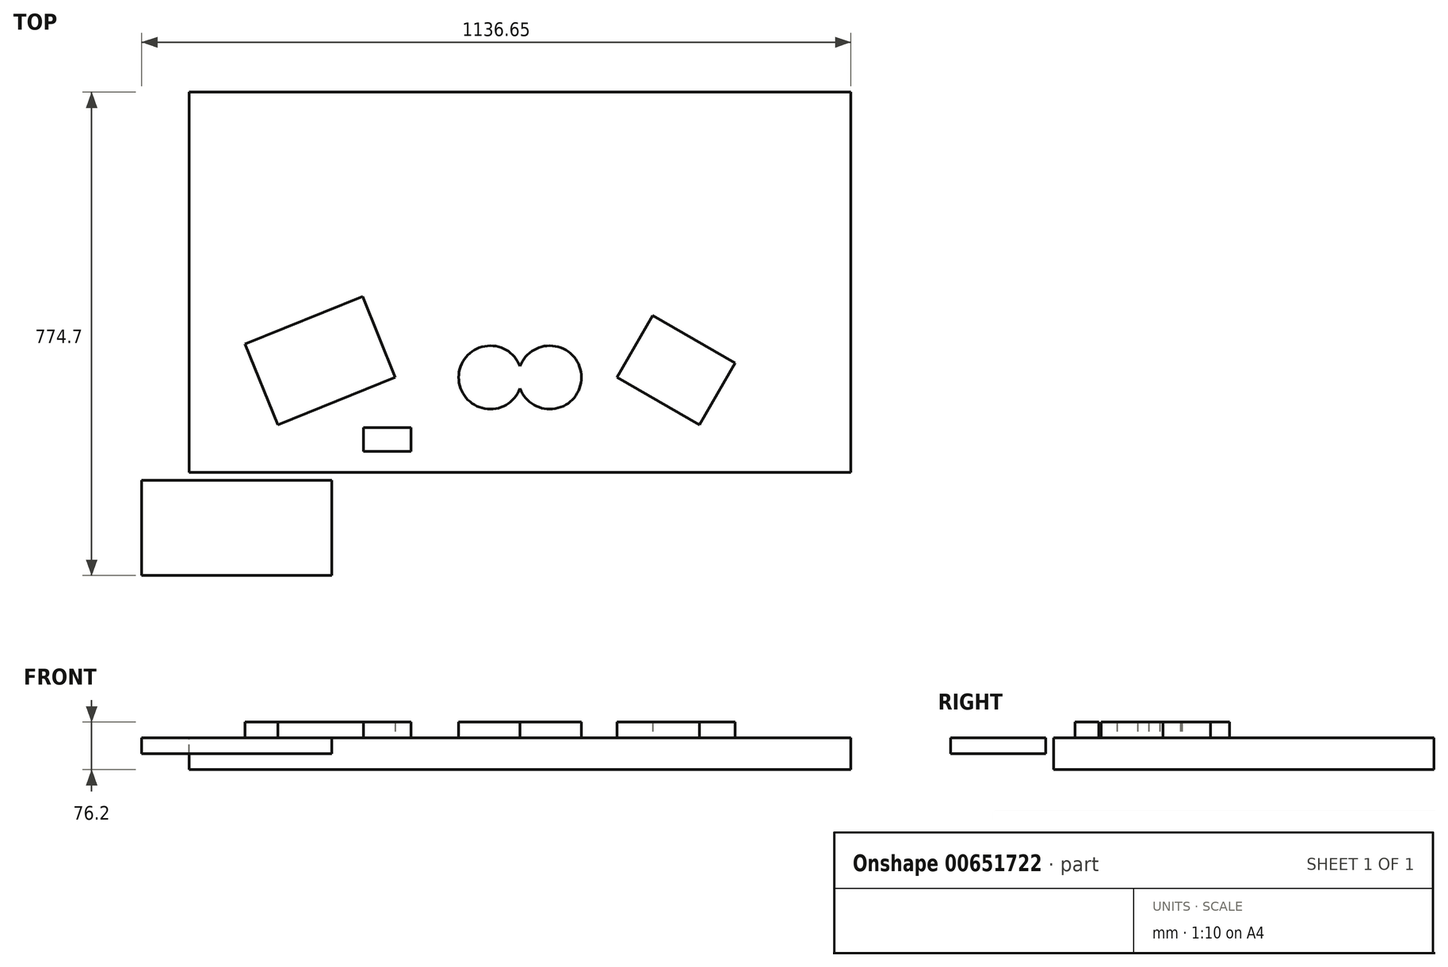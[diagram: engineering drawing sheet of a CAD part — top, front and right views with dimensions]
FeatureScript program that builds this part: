
annotation { "Feature Type Name" : "Feature", "Feature Type Description" : "" }
export const myFeature = defineFeature(function(context is Context, id is Id, definition is map)
    precondition{}
    {
        {
            var Q0;
            Q0=qCreatedBy(makeId("Top.planeOp"),FACE);
            var sketch = newSketch(context, id + "F0", { "sketchPlane" : qUnion([Q0])});
            skLineSegment(sketch, "E0.bottom", {"start": v(0, 0) * mm, "end": v(1060.45, 0) * mm});
            skLineSegment(sketch, "E0.top", {"start": v(0, 609.6) * mm, "end": v(1060.45, 609.6) * mm});
            skLineSegment(sketch, "E0.left", {"start": v(0, 0) * mm, "end": v(0, 609.6) * mm});
            skLineSegment(sketch, "E0.right", {"start": v(1060.45, 0) * mm, "end": v(1060.45, 609.6) * mm});
            skPoint(sketch, "E1", {"position": v(530.22, 0) * mm});
            skPoint(sketch, "E2", {"position": v(1060.45, 124.87) * mm});
            skPoint(sketch, "E3", {"position": v(1060.45, 302.67) * mm});
            skSolve(sketch);
        }
        {
            var Q0;
            Q0=makeQuery(id+"F0.imprint","IMPRINT",FACE,{"disambiguationData":[TD([[makeQuery(id+"F0.imprint","IMPRINT",EDGE,{"derivedFrom":sQuery(id+"F0.wireOp",EDGE,"E0.bottom")}),1.0]])]});
            var sketch = newSketch(context, id + "F1", { "sketchPlane" : qUnion([Q0])});
            skPoint(sketch, "E4", {"position": v(89.44, 205.7) * mm});
            skPoint(sketch, "E5", {"position": v(141.83, 76.2) * mm});
            skPoint(sketch, "E6", {"position": v(330.2, 152.4) * mm});
            skPoint(sketch, "E7", {"position": v(277.81, 281.9) * mm});
            skLineSegment(sketch, "E8", {"start": v(277.81, 281.9) * mm, "end": v(330.2, 152.4) * mm});
            skLineSegment(sketch, "E9", {"start": v(141.83, 76.2) * mm, "end": v(330.2, 152.4) * mm});
            skLineSegment(sketch, "E10", {"start": v(89.44, 205.7) * mm, "end": v(277.81, 281.9) * mm});
            skLineSegment(sketch, "E11", {"start": v(89.44, 205.7) * mm, "end": v(141.83, 76.2) * mm});
            skPoint(sketch, "E12", {"position": v(742.95, 251.39) * mm});
            skPoint(sketch, "E13", {"position": v(685.8, 152.4) * mm});
            skPoint(sketch, "E14", {"position": v(817.78, 76.2) * mm});
            skPoint(sketch, "E15", {"position": v(874.93, 175.19) * mm});
            skLineSegment(sketch, "E16", {"start": v(874.93, 175.19) * mm, "end": v(817.78, 76.2) * mm});
            skLineSegment(sketch, "E17", {"start": v(685.8, 152.4) * mm, "end": v(817.78, 76.2) * mm});
            skLineSegment(sketch, "E18", {"start": v(742.95, 251.39) * mm, "end": v(874.93, 175.19) * mm});
            skLineSegment(sketch, "E19", {"start": v(742.95, 251.39) * mm, "end": v(685.8, 152.4) * mm});
            skPoint(sketch, "E20", {"position": v(482.6, 152.4) * mm});
            skLineSegment(sketch, "E21.bottom", {"start": v(279.01, 72.15) * mm, "end": v(355.21, 72.15) * mm});
            skLineSegment(sketch, "E21.top", {"start": v(279.01, 34.05) * mm, "end": v(355.21, 34.05) * mm});
            skLineSegment(sketch, "E21.left", {"start": v(279.01, 72.15) * mm, "end": v(279.01, 34.05) * mm});
            skLineSegment(sketch, "E21.right", {"start": v(355.21, 72.15) * mm, "end": v(355.21, 34.05) * mm});
            skPoint(sketch, "E22", {"position": v(577.85, 152.4) * mm});
            skArc(sketch, "E23", {"start": v(530.22, 134.72) * mm, "mid": v(628.65, 152.4) * mm, "end": v(530.22, 170.08) * mm});
            skArc(sketch, "E24", {"start": v(530.22, 170.08) * mm, "mid": v(431.8, 152.4) * mm, "end": v(530.22, 134.72) * mm});
            skPoint(sketch, "E25", {"position": v(-76.2, 0) * mm});
            skPoint(sketch, "E26", {"position": v(-76.2, -165.1) * mm});
            skLineSegment(sketch, "E27.bottom", {"start": v(-76.2, -165.1) * mm, "end": v(228.6, -165.1) * mm});
            skLineSegment(sketch, "E27.top", {"start": v(-76.2, -12.7) * mm, "end": v(228.6, -12.7) * mm});
            skLineSegment(sketch, "E27.left", {"start": v(-76.2, -165.1) * mm, "end": v(-76.2, -12.7) * mm});
            skLineSegment(sketch, "E27.right", {"start": v(228.6, -165.1) * mm, "end": v(228.6, -12.7) * mm});
            skSolve(sketch);
        }
        {
            var Q0;
            Q0=makeQuery(id+"F1.imprint","IMPRINT",FACE,{"disambiguationData":[TD([[makeQuery(id+"F1.imprint","IMPRINT",EDGE,{"derivedFrom":sQuery(id+"F1.wireOp",EDGE,"E23")}),1.0]])]});
            var Q1;
            Q1=makeQuery(id+"F1.imprint","IMPRINT",FACE,{"disambiguationData":[TD([[makeQuery(id+"F1.imprint","IMPRINT",EDGE,{"derivedFrom":sQuery(id+"F1.wireOp",EDGE,"E8")}),-1.0]])]});
            var Q2;
            Q2=makeQuery(id+"F1.imprint","IMPRINT",FACE,{"disambiguationData":[TD([[makeQuery(id+"F1.imprint","IMPRINT",EDGE,{"derivedFrom":sQuery(id+"F1.wireOp",EDGE,"E21.bottom")}),-1.0]])]});
            var Q3;
            Q3=makeQuery(id+"F1.imprint","IMPRINT",FACE,{"disambiguationData":[TD([[makeQuery(id+"F1.imprint","IMPRINT",EDGE,{"derivedFrom":sQuery(id+"F1.wireOp",EDGE,"E16")}),-1.0]])]});
            extrude(context, id + "F2", {"entities" : qUnion([Q0, Q1, Q2, Q3]), "depth" : 25.4 * mm, "offsetDistance" : 25.4 * mm});
        }
        {
            var Q0;
            Q0 = qSketchRegion(id + "F0", true);
            extrude(context, id + "F3", {"entities" : qUnion([Q0]), "oppositeDirection" : true, "depth" : 50.8 * mm, "offsetDistance" : 25.4 * mm});
        }
        {
            var Q0;
            Q0=makeQuery(id+"F1.imprint","IMPRINT",FACE,{"disambiguationData":[TD([[makeQuery(id+"F1.imprint","IMPRINT",EDGE,{"derivedFrom":sQuery(id+"F1.wireOp",EDGE,"E27.bottom")}),1.0]])]});
            extrude(context, id + "F4", {"entities" : qUnion([Q0]), "oppositeDirection" : true, "depth" : 25.4 * mm, "offsetDistance" : 25.4 * mm});
        }
    });
